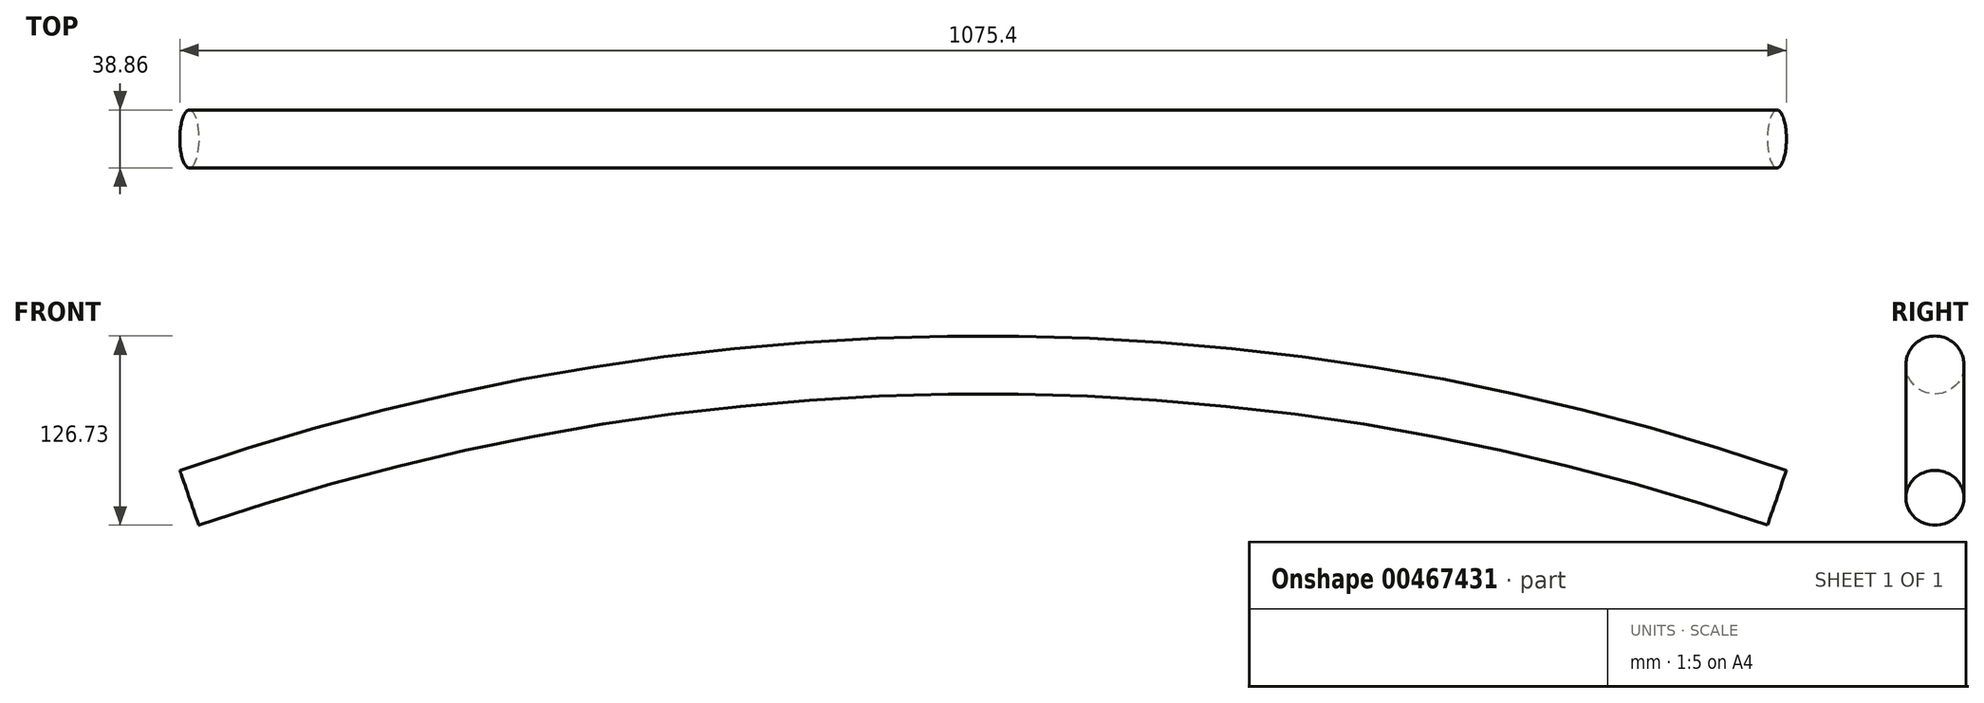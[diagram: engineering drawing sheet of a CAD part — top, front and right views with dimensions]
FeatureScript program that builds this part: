
annotation { "Feature Type Name" : "Feature", "Feature Type Description" : "" }
export const myFeature = defineFeature(function(context is Context, id is Id, definition is map)
    precondition{}
    {
        {
            var Q0;
            Q0=qCreatedBy(makeId("Top.planeOp"),FACE);
            var sketch = newSketch(context, id + "F0", { "sketchPlane" : qUnion([Q0])});
            skLineSegment(sketch, "E0", {"start": v(0, 0) * mm, "end": v(1632.15, 0) * mm});
            skCircle(sketch, "E1", {"center": v(1632.15, 0) * mm, "radius": 19.43 * mm});
            skLineSegment(sketch, "E2", {"start": v(0, 18.17) * mm, "end": v(0, -26.19) * mm});
            skSolve(sketch);
        }
        {
            var Q0;
            Q0=makeQuery(id+"F0.imprint","IMPRINT",FACE,{"disambiguationData":[TD([[makeQuery(id+"F0.imprint","IMPRINT",EDGE,{"derivedFrom":sQuery(id+"F0.wireOp",EDGE,"E1")}),1.0]])]});
            var Q1;
            Q1=sQuery(id+"F0.wireOp",EDGE,"E2");
            revolve(context, id + "F1", {"entities" : qUnion([Q0]), "axis" : qUnion([Q1]), "revolveType" : RevolveType.TWO_DIRECTIONS, "oppositeDirection" : true, "angle" : 289 * degree, "angleBack" : 251 * degree});
        }
    });
